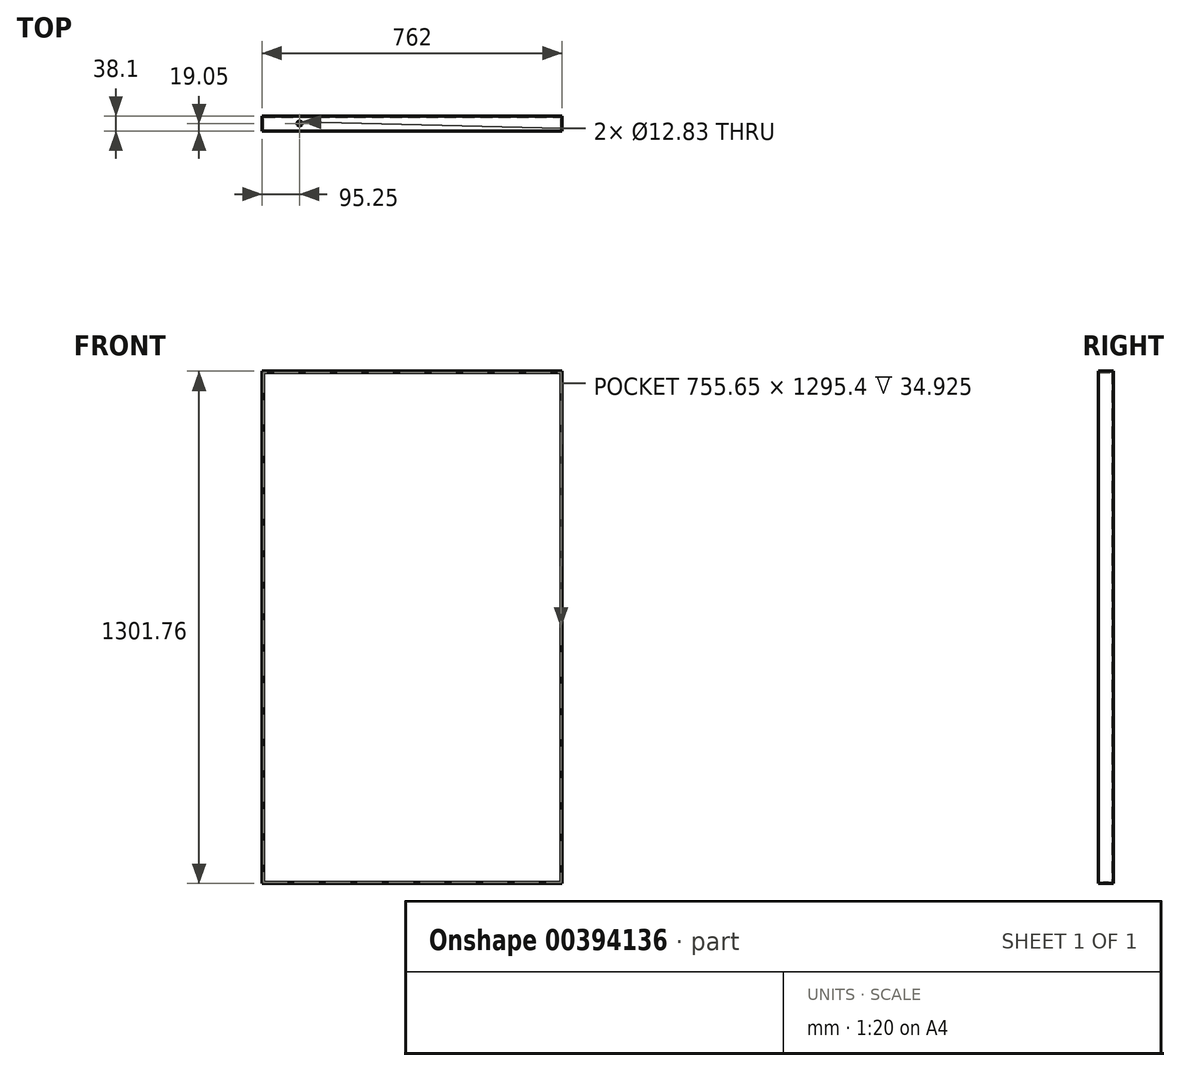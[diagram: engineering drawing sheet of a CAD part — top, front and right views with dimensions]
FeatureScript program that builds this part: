
annotation { "Feature Type Name" : "Feature", "Feature Type Description" : "" }
export const myFeature = defineFeature(function(context is Context, id is Id, definition is map)
    precondition{}
    {
        {
            var Q0;
            Q0=qCreatedBy(makeId("Front.planeOp"),FACE);
            var sketch = newSketch(context, id + "F0", { "sketchPlane" : qUnion([Q0])});
            skLineSegment(sketch, "E0.bottom", {"start": v(-381, 650.88) * mm, "end": v(381, 650.88) * mm});
            skLineSegment(sketch, "E0.top", {"start": v(-381, -650.88) * mm, "end": v(381, -650.88) * mm});
            skLineSegment(sketch, "E0.left", {"start": v(-381, 650.88) * mm, "end": v(-381, -650.88) * mm});
            skLineSegment(sketch, "E0.right", {"start": v(381, 650.88) * mm, "end": v(381, -650.88) * mm});
            skSolve(sketch);
        }
        {
            var Q0;
            Q0 = qSketchRegion(id + "F0", true);
            extrude(context, id + "F1", {"entities" : qUnion([Q0]), "depth" : 38.1 * mm});
        }
        {
            var Q0;
            Q0=makeQuery(id+"F1.opExtrude","CAP_FACE",FACE,{"disambiguationData":[OSD([sQuery(id+"F0.wireOp",EDGE,"E0.bottom"),sQuery(id+"F0.wireOp",EDGE,"E0.top"),sQuery(id+"F0.wireOp",EDGE,"E0.left"),sQuery(id+"F0.wireOp",EDGE,"E0.right")])],"isStart":false});
            shell(context, id + "F2", {"entities" : qUnion([Q0]), "thickness" : 3.17 * mm});
        }
        {
            var Q0;
            Q0=makeQuery(id+"F1.opExtrude","SWEPT_FACE",FACE,{"disambiguationData":[OSD([sQuery(id+"F0.wireOp",EDGE,"E0.bottom")])]});
            var sketch = newSketch(context, id + "F3", { "sketchPlane" : qUnion([Q0])});
            skCircle(sketch, "E1", {"center": v(-285.75, -19.05) * mm, "radius": 6.41 * mm});
            skSolve(sketch);
        }
        {
            var Q0;
            Q0 = qSketchRegion(id + "F3", true);
            extrude(context, id + "F4", {"entities" : qUnion([Q0]), "operationType" : NewBodyOperationType.REMOVE, "endBound" : BoundingType.THROUGH_ALL, "oppositeDirection" : true, "depth" : 25.4 * mm});
        }
    });
